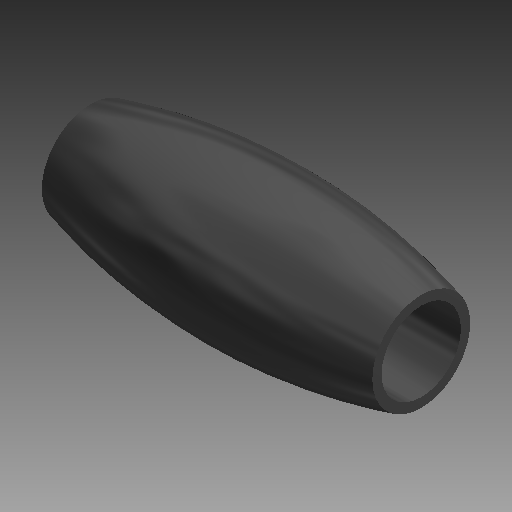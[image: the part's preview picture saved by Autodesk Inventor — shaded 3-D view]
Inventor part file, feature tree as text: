
AUTODESK INVENTOR PART (.ipt)
format: ipt  version: 2019 (Build 230136000, 136)  size: 102,400 bytes
history: native  units: mm (DEFAULTED — no unit token found)
features: revolve x1
ambient origin geometry x8: Origin, YZ Plane, XZ Plane, XY Plane, X Axis, Y Axis, Z Axis, Center Point
bodies: Solid1 (feature_tree)
feature tree (1):
  revolve  "Revolve1"  [1 undecoded]
note: 1 required parameter value undecoded (feature->parameter linkage not recoverable at this tier; creation-order binding heuristic only, values carry confidence <= 0.55)
